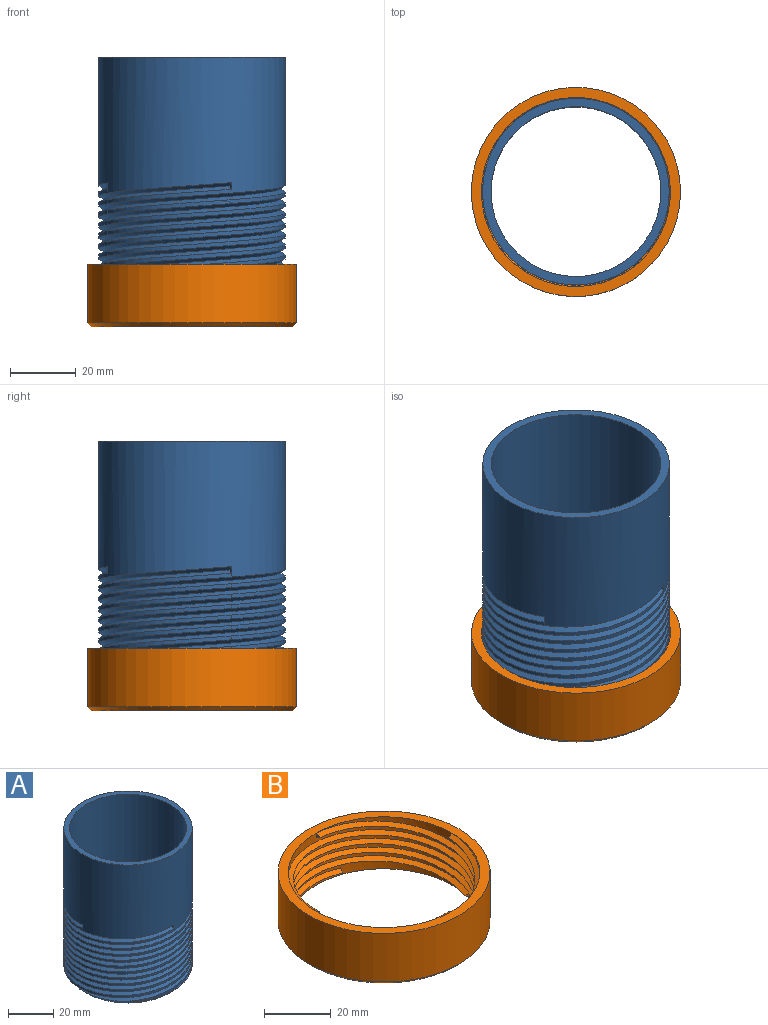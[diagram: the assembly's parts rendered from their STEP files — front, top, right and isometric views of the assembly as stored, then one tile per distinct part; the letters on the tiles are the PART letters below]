
ASSEMBLY  parts=2 mates=1
PART A: 27 faces, bbox 56.6x56.6x76.6 mm
  f0: cylinder r=25.78mm len=76.2mm, axis (0,0,1), area 12343.4mm2, adj f13,f14
  f1: cylinder r=28.32mm len=56.64mm, axis (0,0,1), area 124.9mm2, adj f2,f14,f19,f26
  f2: cylinder r=28.32mm len=56.64mm, axis (0,0,1), area 209.3mm2, adj f1,f3,f19,f26
  f3: cylinder r=28.32mm len=56.64mm, axis (0,0,1), area 208.9mm2, adj f2,f4,f19,f26
  f4: cylinder r=28.32mm len=56.64mm, axis (0,0,1), area 7375.8mm2, adj f3,f5,f8,f11,f13,f15,f16,f17
  f5: cylinder r=28.32mm len=56.64mm, axis (0,0,1), area 208.6mm2, adj f4,f6,f23,f25
  f6: cylinder r=28.32mm len=56.64mm, axis (0,0,1), area 209mm2, adj f5,f7,f23,f25
  f7: cylinder r=28.32mm len=50.49mm, axis (0,0,1), area 72.4mm2, adj f6,f14,f23,f25
  f8: cylinder r=28.32mm len=56.64mm, axis (0,0,1), area 209mm2, adj f4,f9,f17,f22
  f9: cylinder r=28.32mm len=56.64mm, axis (0,0,1), area 209mm2, adj f8,f10,f17,f22
  f10: cylinder r=28.32mm len=22.17mm, axis (0,0,1), area 20.2mm2, adj f9,f14,f17,f22
  f11: cylinder r=28.32mm len=56.64mm, axis (0,0,1), area 209.4mm2, adj f4,f12,f16,f20
  f12: cylinder r=28.32mm len=56.64mm, axis (0,0,1), area 177.3mm2, adj f11,f14,f16,f20
  f13: plane 56.64x56.64mm, normal (0,0,1), area 431.7mm2, adj f0,f4
  f14: cone r=28.32mm half-angle=45deg, axis (0,0,1), area 476.3mm2, adj f0,f1,f7,f10,f12,f16,f17,f19
  f15: plane 2x1.73mm, normal (-1,0,0), area 1.7mm2, adj f4,f16,f17
  f16: bspline ~56.64x56.64mm, area 949.7mm2, adj f4,f11,f12,f14,f15,f17
  f17: bspline ~56.64x56.64mm, area 977.7mm2, adj f4,f8,f9,f10,f14,f15,f16
  f18: plane 2x1.73mm, normal (0,-1,0), area 1.7mm2, adj f4,f19,f20
  f19: bspline ~56.64x56.64mm, area 949.7mm2, adj f1,f2,f3,f14,f18,f20
  f20: bspline ~56.64x56.64mm, area 977.7mm2, adj f4,f11,f12,f14,f18,f19
  f21: plane 2x1.73mm, normal (0,1,0), area 1.7mm2, adj f4,f22,f23
  f22: bspline ~56.64x56.64mm, area 949.7mm2, adj f4,f8,f9,f10,f14,f21,f23
  f23: bspline ~56.64x56.64mm, area 977.7mm2, adj f4,f5,f6,f7,f14,f21,f22
  f24: plane 2x1.73mm, normal (1,0,0), area 1.7mm2, adj f4,f25,f26
  f25: bspline ~56.64x56.64mm, area 949.7mm2, adj f4,f5,f6,f7,f14,f24,f26
  f26: bspline ~56.64x56.64mm, area 977.7mm2, adj f1,f2,f3,f4,f14,f24,f25
PART B: 26 faces, bbox 63.5x63.5x19.3 mm
  f0: cylinder r=28.7mm len=57.4mm, axis (0,0,1), area 840.4mm2, adj f1,f2,f4,f5,f8,f10,f11,f12
  f1: cylinder r=28.7mm len=57.4mm, axis (0,0,1), area 133.6mm2, adj f0,f7,f17,f20,f24
  f2: cylinder r=28.7mm len=57.4mm, axis (0,0,1), area 248mm2, adj f0,f3,f16,f19
  f3: cylinder r=28.7mm len=28.7mm, axis (0,0,1), area 71.6mm2, adj f2,f7,f13,f19
  f4: cylinder r=28.7mm len=57.4mm, axis (0,0,1), area 257.5mm2, adj f0,f7,f9,f12,f15
  f5: cylinder r=28.7mm len=57.4mm, axis (0,0,1), area 195.6mm2, adj f0,f7,f11,f21,f23
  f6: cylinder r=31.75mm len=63.5mm, axis (0,0,-1), area 3547mm2, adj f7,f25
  f7: plane 63.5x63.5mm, normal (0,0,1), area 578.9mm2, adj f1,f3,f4,f5,f6
  f8: plane 60.96x60.96mm, normal (0,0,-1), area 330.6mm2, adj f0,f25
  f9: plane 1.8x1.56mm, normal (1,0,0), area 1.4mm2, adj f4,f11,f12
  f10: plane 1.81x1.49mm, normal (0.31,0.95,0), area 1.4mm2, adj f0,f11,f12
  f11: bspline ~57.4x57.4mm, area 411.2mm2, adj f0,f5,f9,f10,f12
  f12: bspline ~57.4x57.4mm, area 411.3mm2, adj f0,f4,f9,f10,f11
  f13: plane 1.8x1.56mm, normal (0,1,0), area 1.4mm2, adj f3,f15,f16
  f14: plane 1.81x1.49mm, normal (-0.95,0.31,0), area 1.4mm2, adj f0,f15,f16
  f15: bspline ~57.4x57.4mm, area 411.2mm2, adj f0,f4,f13,f14,f16
  f16: bspline ~57.4x57.4mm, area 411.3mm2, adj f0,f2,f13,f14,f15
  f17: plane 1.8x1.56mm, normal (-1,0,0), area 1.4mm2, adj f1,f19,f20
  f18: plane 1.81x1.49mm, normal (-0.31,-0.95,0), area 1.4mm2, adj f0,f19,f20
  f19: bspline ~57.4x57.4mm, area 411.2mm2, adj f0,f2,f3,f17,f18,f20
  f20: bspline ~57.4x57.4mm, area 411.3mm2, adj f0,f1,f17,f18,f19
  f21: plane 1.8x1.56mm, normal (0,-1,0), area 1.4mm2, adj f5,f23,f24
  f22: plane 1.81x1.49mm, normal (0.95,-0.31,0), area 1.4mm2, adj f0,f23,f24
  f23: bspline ~57.4x57.4mm, area 411.3mm2, adj f0,f5,f21,f22,f24
  f24: bspline ~57.4x57.4mm, area 411.2mm2, adj f0,f1,f21,f22,f23
  f25: cone r=31.75mm half-angle=45deg, axis (0,0,1), area 351.1mm2, adj f6,f8
PLACE A rot(axis=(0,0,-1),154.8deg) t=(20.72,-16.96,62.49)mm
PLACE B rot(axis=(0,0,1),133.8deg) t=(20.72,-16.96,25.05)mm fixed
MATE cylindrical A.f0 <-> B.f0  axis (0,0,1) through (20.72,-16.96,37.09)mm
